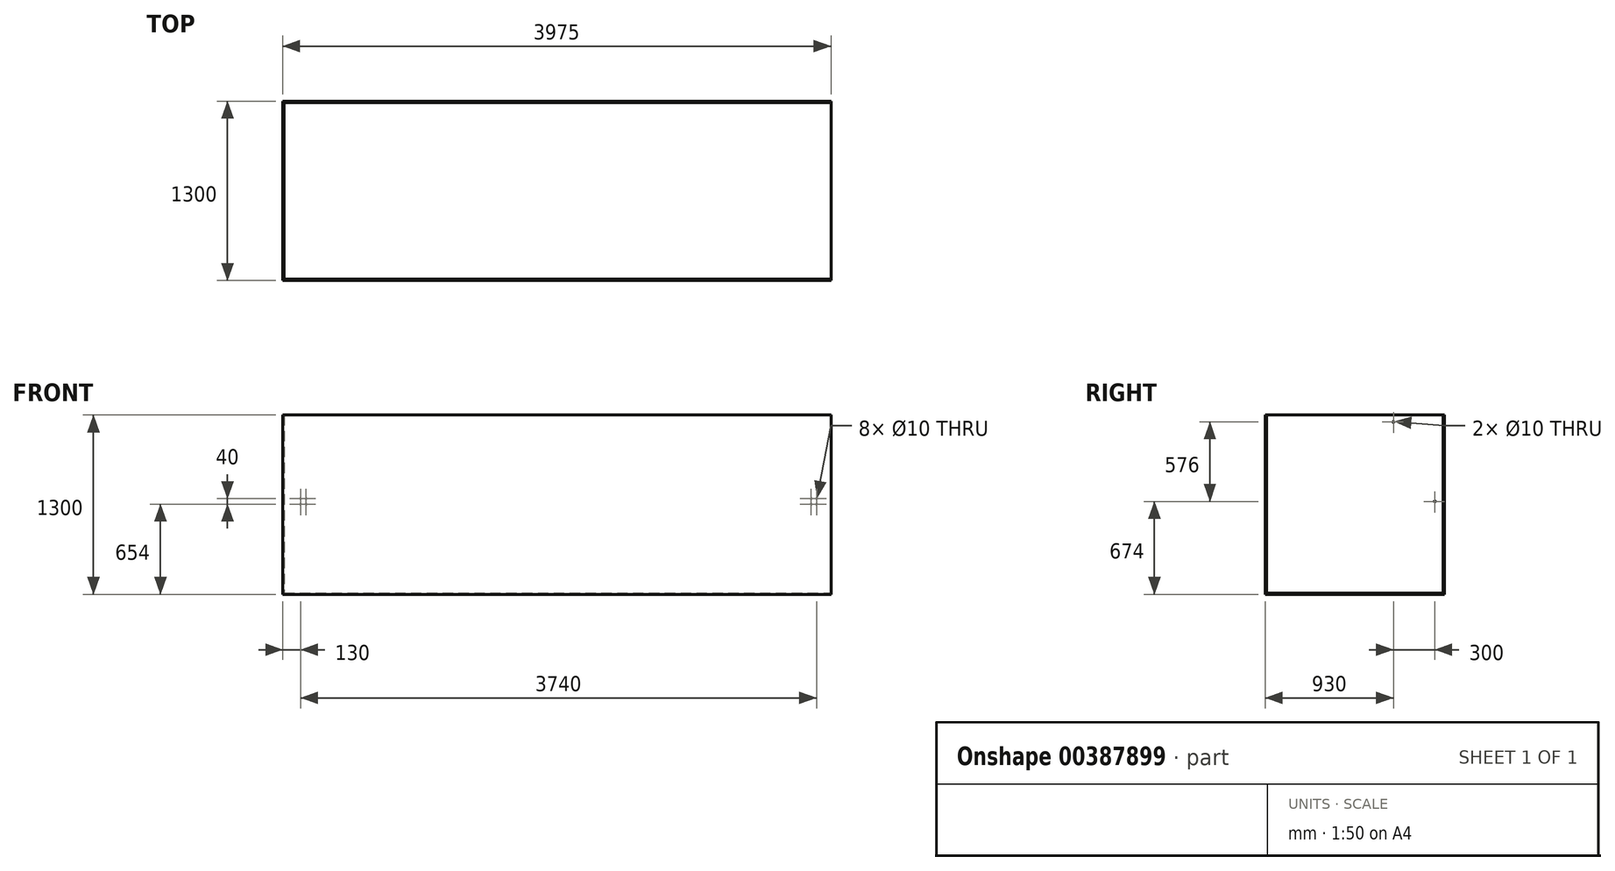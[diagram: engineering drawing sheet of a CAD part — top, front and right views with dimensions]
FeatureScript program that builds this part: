
annotation { "Feature Type Name" : "Feature", "Feature Type Description" : "" }
export const myFeature = defineFeature(function(context is Context, id is Id, definition is map)
    precondition{}
    {
        {
            var Q0;
            Q0=qCreatedBy(makeId("Front.planeOp"),FACE);
            var sketch = newSketch(context, id + "F0", { "sketchPlane" : qUnion([Q0])});
            skLineSegment(sketch, "E0.bottom", {"start": v(-2000, 650) * mm, "end": v(2000, 650) * mm});
            skLineSegment(sketch, "E0.top", {"start": v(-2000, -650) * mm, "end": v(2000, -650) * mm});
            skLineSegment(sketch, "E0.left", {"start": v(-2000, 650) * mm, "end": v(-2000, -650) * mm});
            skLineSegment(sketch, "E0.right", {"start": v(2000, 650) * mm, "end": v(2000, -650) * mm});
            skPoint(sketch, "E0.middle", {"position": v(0, 0) * mm});
            skSolve(sketch);
        }
        {
            var Q0;
            Q0 = qSketchRegion(id + "F0", true);
            extrude(context, id + "F1", {"entities" : qUnion([Q0]), "depth" : 1300 * mm, "symmetric" : true});
        }
        {
            var Q0;
            Q0=makeQuery(id+"F1.opExtrude","SWEPT_FACE",FACE,{"disambiguationData":[OSD([sQuery(id+"F0.wireOp",EDGE,"E0.bottom")])]});
            shell(context, id + "F2", {"entities" : qUnion([Q0]), "thickness" : 10 * mm});
        }
        {
            var Q0;
            Q0=makeQuery(id+"F1.opExtrude","SWEPT_FACE",FACE,{"disambiguationData":[OSD([sQuery(id+"F0.wireOp",EDGE,"E0.left")])]});
            var sketch = newSketch(context, id + "F3", { "sketchPlane" : qUnion([Q0])});
            skLineSegment(sketch, "E1", {"start": v(-650, 650) * mm, "end": v(-580, 650) * mm});
            skLineSegment(sketch, "E2", {"start": v(-580, 650) * mm, "end": v(-580, 24) * mm});
            skLineSegment(sketch, "E3", {"start": v(-650, 650) * mm, "end": v(-280, 650) * mm});
            skLineSegment(sketch, "E4", {"start": v(-280, 650) * mm, "end": v(-280, 600) * mm});
            skSolve(sketch);
        }
        {
            var Q0;
            Q0=sQuery(id+"F3.wireOp",VERTEX,"E2.end");
            var Q1;
            Q1=makeQuery(id+"F1.opExtrude","SWEPT_BODY",BODY,{"disambiguationData":[OSD([sQuery(id+"F0.wireOp",EDGE,"E0.bottom"),sQuery(id+"F0.wireOp",EDGE,"E0.top"),sQuery(id+"F0.wireOp",EDGE,"E0.left"),sQuery(id+"F0.wireOp",EDGE,"E0.right")])]});
            hole(context, id + "F4", {"style" : HoleStyle.SIMPLE, "endStyle" : HoleEndStyle.THROUGH, "holeDiameter" : 10 * mm, "isTappedThrough" : true, "tappedDepth" : 12 * mm, "tapClearance" : 3, "locations" : qUnion([Q0]), "scope" : qUnion([Q1])});
        }
        {
            var Q0;
            Q0=sQuery(id+"F3.wireOp",VERTEX,"E4.end");
            var Q1;
            Q1=makeQuery(id+"F1.opExtrude","SWEPT_BODY",BODY,{"disambiguationData":[OSD([sQuery(id+"F0.wireOp",EDGE,"E0.bottom"),sQuery(id+"F0.wireOp",EDGE,"E0.top"),sQuery(id+"F0.wireOp",EDGE,"E0.left"),sQuery(id+"F0.wireOp",EDGE,"E0.right")])]});
            hole(context, id + "F5", {"style" : HoleStyle.SIMPLE, "endStyle" : HoleEndStyle.THROUGH, "holeDiameter" : 10 * mm, "isTappedThrough" : true, "tappedDepth" : 12 * mm, "tapClearance" : 3, "locations" : qUnion([Q0]), "scope" : qUnion([Q1])});
        }
        {
            var Q0;
            {var subQ0=sQuery(id+"F0.wireOp",EDGE,"E0.right");var subQ1=sQuery(id+"F0.wireOp",EDGE,"E0.left");var subQ2=sQuery(id+"F0.wireOp",EDGE,"E0.top");var subQ3=sQuery(id+"F0.wireOp",EDGE,"E0.bottom");Q0=makeQuery(id+"F2.opShell","OFFSET_FACE",FACE,{"disambiguationData":[OSD([subQ3,subQ2,subQ1,subQ0]),TDD([makeQuery(id+"F1.opExtrude","CAP_FACE",FACE,{"disambiguationData":[OSD([subQ3,subQ2,subQ1,subQ0])],"isStart":true})])]});}
            var sketch = newSketch(context, id + "F6", { "sketchPlane" : qUnion([Q0])});
            skLineSegment(sketch, "E5", {"start": v(-1990, 650) * mm, "end": v(-1850, 650) * mm});
            skLineSegment(sketch, "E6", {"start": v(-1850, 650) * mm, "end": v(-1850, 24) * mm});
            skLineSegment(sketch, "E7.bottom", {"start": v(-1870, 44) * mm, "end": v(-1830, 44) * mm});
            skLineSegment(sketch, "E7.top", {"start": v(-1870, 4) * mm, "end": v(-1830, 4) * mm});
            skLineSegment(sketch, "E7.left", {"start": v(-1870, 44) * mm, "end": v(-1870, 4) * mm});
            skLineSegment(sketch, "E7.right", {"start": v(-1830, 44) * mm, "end": v(-1830, 4) * mm});
            skPoint(sketch, "E7.middle", {"position": v(-1850, 24) * mm});
            skCircle(sketch, "E8", {"center": v(-1870, 44) * mm, "radius": 5 * mm});
            skCircle(sketch, "E9", {"center": v(-1830, 44) * mm, "radius": 5 * mm});
            skCircle(sketch, "E10", {"center": v(-1830, 4) * mm, "radius": 5 * mm});
            skCircle(sketch, "E11", {"center": v(-1870, 4) * mm, "radius": 5 * mm});
            skLineSegment(sketch, "E12", {"start": v(1990, 650) * mm, "end": v(1850, 650) * mm});
            skLineSegment(sketch, "E13", {"start": v(1850, 650) * mm, "end": v(1850, 24) * mm});
            skLineSegment(sketch, "E14.bottom", {"start": v(1830, 44) * mm, "end": v(1870, 44) * mm});
            skLineSegment(sketch, "E14.top", {"start": v(1830, 4) * mm, "end": v(1870, 4) * mm});
            skLineSegment(sketch, "E14.left", {"start": v(1830, 44) * mm, "end": v(1830, 4) * mm});
            skLineSegment(sketch, "E14.right", {"start": v(1870, 44) * mm, "end": v(1870, 4) * mm});
            skPoint(sketch, "E14.middle", {"position": v(1850, 24) * mm});
            skSolve(sketch);
        }
        {
            var Q0;
            Q0=sQuery(id+"F6.wireOp",VERTEX,"E7.left.start");
            var Q1;
            Q1=sQuery(id+"F6.wireOp",VERTEX,"E7.right.start");
            var Q2;
            Q2=sQuery(id+"F6.wireOp",VERTEX,"E7.right.end");
            var Q3;
            Q3=sQuery(id+"F6.wireOp",VERTEX,"E11.center");
            var Q4;
            Q4=makeQuery(id+"F1.opExtrude","SWEPT_BODY",BODY,{"disambiguationData":[OSD([sQuery(id+"F0.wireOp",EDGE,"E0.bottom"),sQuery(id+"F0.wireOp",EDGE,"E0.top"),sQuery(id+"F0.wireOp",EDGE,"E0.left"),sQuery(id+"F0.wireOp",EDGE,"E0.right")])]});
            hole(context, id + "F7", {"style" : HoleStyle.SIMPLE, "endStyle" : HoleEndStyle.THROUGH, "holeDiameter" : 10 * mm, "isTappedThrough" : true, "tappedDepth" : 12 * mm, "tapClearance" : 3, "locations" : qUnion([Q0, Q1, Q2, Q3]), "scope" : qUnion([Q4])});
        }
        {
            var Q0;
            Q0=sQuery(id+"F6.wireOp",VERTEX,"E14.bottom.start");
            var Q1;
            Q1=sQuery(id+"F6.wireOp",VERTEX,"E14.right.start");
            var Q2;
            Q2=sQuery(id+"F6.wireOp",VERTEX,"E14.right.end");
            var Q3;
            Q3=sQuery(id+"F6.wireOp",VERTEX,"E14.top.start");
            var Q4;
            Q4=makeQuery(id+"F1.opExtrude","SWEPT_BODY",BODY,{"disambiguationData":[OSD([sQuery(id+"F0.wireOp",EDGE,"E0.bottom"),sQuery(id+"F0.wireOp",EDGE,"E0.top"),sQuery(id+"F0.wireOp",EDGE,"E0.left"),sQuery(id+"F0.wireOp",EDGE,"E0.right")])]});
            hole(context, id + "F8", {"style" : HoleStyle.SIMPLE, "endStyle" : HoleEndStyle.THROUGH, "holeDiameter" : 10 * mm, "isTappedThrough" : true, "tappedDepth" : 12 * mm, "tapClearance" : 3, "locations" : qUnion([Q0, Q1, Q2, Q3]), "scope" : qUnion([Q4])});
        }
        {
            var Q0;
            Q0=makeQuery(id+"F1.opExtrude","SWEPT_FACE",FACE,{"disambiguationData":[OSD([sQuery(id+"F0.wireOp",EDGE,"E0.right")])]});
            extrude(context, id + "F9", {"entities" : qUnion([Q0]), "operationType" : NewBodyOperationType.REMOVE, "oppositeDirection" : true, "depth" : 25 * mm});
        }
    });
